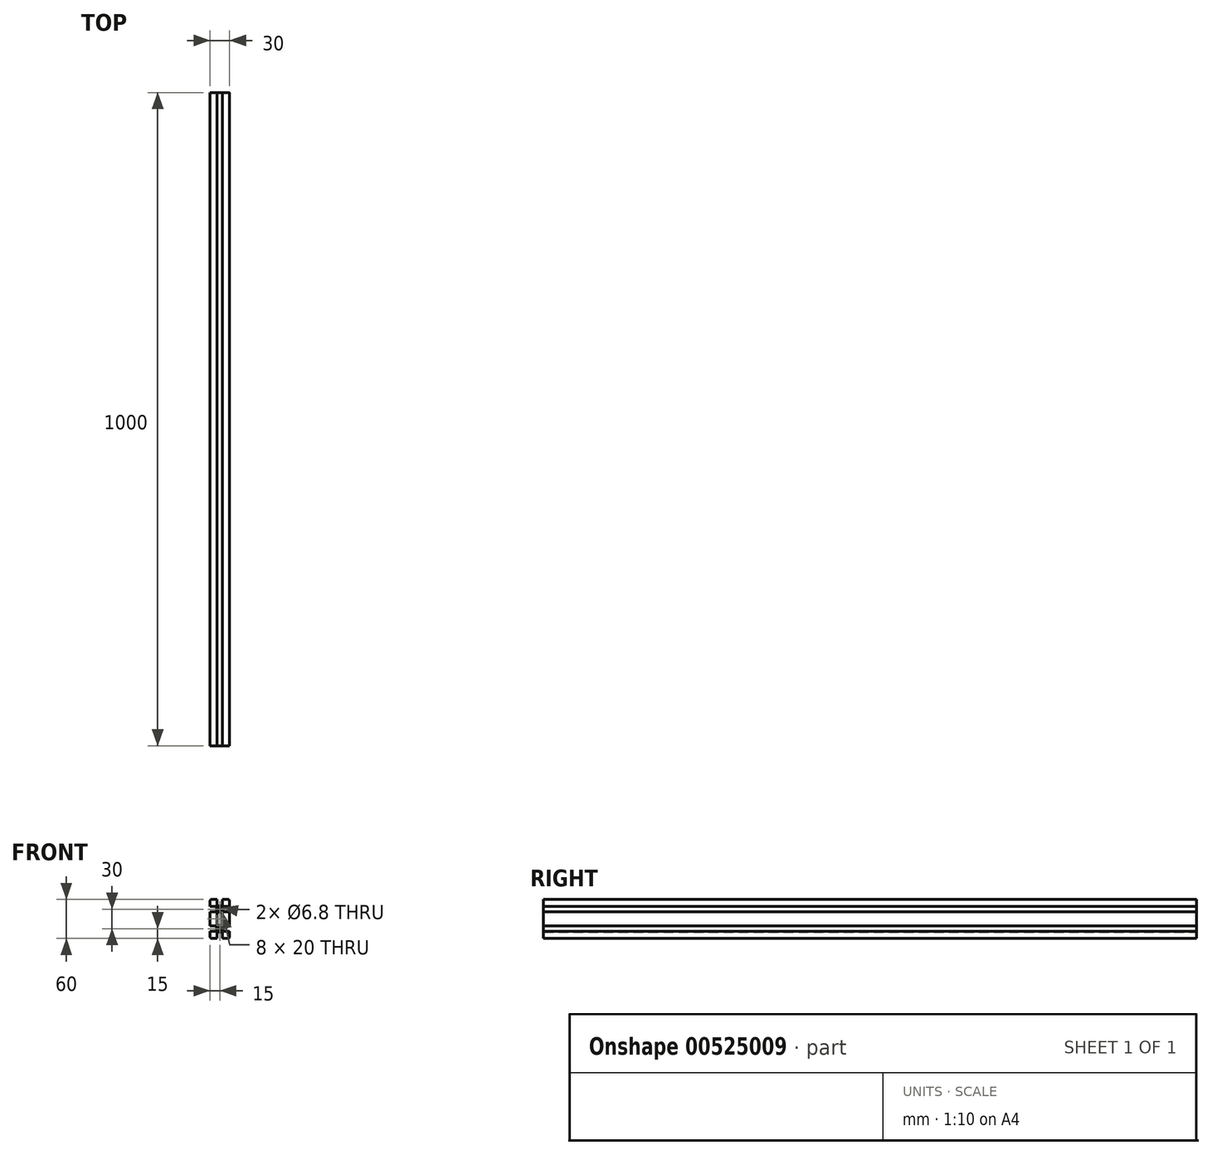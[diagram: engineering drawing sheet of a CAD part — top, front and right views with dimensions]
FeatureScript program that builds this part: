
annotation { "Feature Type Name" : "Feature", "Feature Type Description" : "" }
export const myFeature = defineFeature(function(context is Context, id is Id, definition is map)
    precondition{}
    {
        {
            var Q0;
            Q0=qCreatedBy(makeId("Front.planeOp"),FACE);
            var sketch = newSketch(context, id + "F0", { "sketchPlane" : qUnion([Q0])});
            skLineSegment(sketch, "E0.bottom", {"start": v(15, 30) * mm, "end": v(4, 30) * mm});
            skLineSegment(sketch, "E0.top", {"start": v(15, -30) * mm, "end": v(4, -30) * mm});
            skLineSegment(sketch, "E0.left", {"start": v(15, 30) * mm, "end": v(15, 19) * mm});
            skLineSegment(sketch, "E0.right", {"start": v(-15, 30) * mm, "end": v(-15, 19) * mm});
            skPoint(sketch, "E0.middle", {"position": v(0, 0) * mm});
            skLineSegment(sketch, "E1.top", {"start": v(-4, 20) * mm, "end": v(4, 20) * mm});
            skLineSegment(sketch, "E1.left", {"start": v(-4, 30) * mm, "end": v(-4, 20) * mm});
            skLineSegment(sketch, "E1.right", {"start": v(4, 30) * mm, "end": v(4, 20) * mm});
            skLineSegment(sketch, "E2.bottom", {"start": v(-15, 19) * mm, "end": v(-5, 19) * mm});
            skLineSegment(sketch, "E2.top", {"start": v(-15, 11) * mm, "end": v(-5, 11) * mm});
            skLineSegment(sketch, "E2.right", {"start": v(-5, 19) * mm, "end": v(-5, 11) * mm});
            skLineSegment(sketch, "E3.bottom", {"start": v(-15, -11) * mm, "end": v(-5, -11) * mm});
            skLineSegment(sketch, "E3.top", {"start": v(-15, -19) * mm, "end": v(-5, -19) * mm});
            skLineSegment(sketch, "E3.right", {"start": v(-5, -11) * mm, "end": v(-5, -19) * mm});
            skLineSegment(sketch, "E4.bottom", {"start": v(15, -11) * mm, "end": v(5, -11) * mm});
            skLineSegment(sketch, "E4.top", {"start": v(15, -19) * mm, "end": v(5, -19) * mm});
            skLineSegment(sketch, "E4.right", {"start": v(5, -11) * mm, "end": v(5, -19) * mm});
            skLineSegment(sketch, "E5.top", {"start": v(-4, -20) * mm, "end": v(4, -20) * mm});
            skLineSegment(sketch, "E5.left", {"start": v(-4, -30) * mm, "end": v(-4, -20) * mm});
            skLineSegment(sketch, "E5.right", {"start": v(4, -30) * mm, "end": v(4, -20) * mm});
            skLineSegment(sketch, "E6.bottom", {"start": v(15, 19) * mm, "end": v(5, 19) * mm});
            skLineSegment(sketch, "E6.top", {"start": v(15, 11) * mm, "end": v(5, 11) * mm});
            skLineSegment(sketch, "E6.right", {"start": v(5, 19) * mm, "end": v(5, 11) * mm});
            skLineSegment(sketch, "E7.trimOffspring", {"start": v(-15, -19) * mm, "end": v(-15, -30) * mm});
            skLineSegment(sketch, "E8.trimOffspring", {"start": v(-15, 11) * mm, "end": v(-15, -11) * mm});
            skLineSegment(sketch, "E9.trimOffspring", {"start": v(-4, 30) * mm, "end": v(-15, 30) * mm});
            skLineSegment(sketch, "E10.trimOffspring", {"start": v(15, 11) * mm, "end": v(15, -11) * mm});
            skLineSegment(sketch, "E11.trimOffspring", {"start": v(15, -19) * mm, "end": v(15, -30) * mm});
            skLineSegment(sketch, "E12.trimOffspring", {"start": v(-4, -30) * mm, "end": v(-15, -30) * mm});
            skSolve(sketch);
        }
        {
            var Q0;
            Q0 = qSketchRegion(id + "F0", true);
            extrude(context, id + "F1", {"entities" : qUnion([Q0]), "endBound" : BoundingType.SYMMETRIC, "depth" : 1000 * mm, "offsetDistance" : 25 * mm});
        }
        {
            var Q0;
            Q0=makeQuery(id+"F1.opExtrude","CAP_FACE",FACE,{"disambiguationData":[OSD([sQuery(id+"F0.wireOp",EDGE,"E0.bottom"),sQuery(id+"F0.wireOp",EDGE,"E0.top"),sQuery(id+"F0.wireOp",EDGE,"E0.left"),sQuery(id+"F0.wireOp",EDGE,"E0.right"),sQuery(id+"F0.wireOp",EDGE,"E1.top"),sQuery(id+"F0.wireOp",EDGE,"E1.left"),sQuery(id+"F0.wireOp",EDGE,"E1.right"),sQuery(id+"F0.wireOp",EDGE,"E2.bottom"),sQuery(id+"F0.wireOp",EDGE,"E2.top"),sQuery(id+"F0.wireOp",EDGE,"E2.right"),sQuery(id+"F0.wireOp",EDGE,"E3.bottom"),sQuery(id+"F0.wireOp",EDGE,"E3.top"),sQuery(id+"F0.wireOp",EDGE,"E3.right"),sQuery(id+"F0.wireOp",EDGE,"E4.bottom"),sQuery(id+"F0.wireOp",EDGE,"E4.top"),sQuery(id+"F0.wireOp",EDGE,"E4.right"),sQuery(id+"F0.wireOp",EDGE,"E5.top"),sQuery(id+"F0.wireOp",EDGE,"E5.left"),sQuery(id+"F0.wireOp",EDGE,"E5.right"),sQuery(id+"F0.wireOp",EDGE,"E6.bottom"),sQuery(id+"F0.wireOp",EDGE,"E6.top"),sQuery(id+"F0.wireOp",EDGE,"E6.right"),sQuery(id+"F0.wireOp",EDGE,"E7.trimOffspring"),sQuery(id+"F0.wireOp",EDGE,"E8.trimOffspring"),sQuery(id+"F0.wireOp",EDGE,"E9.trimOffspring"),sQuery(id+"F0.wireOp",EDGE,"E10.trimOffspring"),sQuery(id+"F0.wireOp",EDGE,"E11.trimOffspring"),sQuery(id+"F0.wireOp",EDGE,"E12.trimOffspring")])],"isStart":false});
            var sketch = newSketch(context, id + "F2", { "sketchPlane" : qUnion([Q0])});
            skPoint(sketch, "E13.centerSnap0", {"position": v(0, 20) * mm});
            skCircle(sketch, "E14", {"center": v(0, -15) * mm, "radius": 3.4 * mm});
            skLineSegment(sketch, "E15.bottom", {"start": v(4, 10) * mm, "end": v(-4, 10) * mm});
            skLineSegment(sketch, "E15.top", {"start": v(4, -10) * mm, "end": v(-4, -10) * mm});
            skLineSegment(sketch, "E15.left", {"start": v(4, 10) * mm, "end": v(4, -10) * mm});
            skLineSegment(sketch, "E15.right", {"start": v(-4, 10) * mm, "end": v(-4, -10) * mm});
            skPoint(sketch, "E15.middle", {"position": v(0, 0) * mm});
            skPoint(sketch, "E13.center.orphan", {"position": v(0, 15.6) * mm});
            skCircle(sketch, "E16", {"center": v(0, 15) * mm, "radius": 3.4 * mm});
            skSolve(sketch);
        }
        {
            var Q0;
            Q0 = qSketchRegion(id + "F2", true);
            extrude(context, id + "F3", {"entities" : qUnion([Q0]), "operationType" : NewBodyOperationType.REMOVE, "oppositeDirection" : true, "depth" : 1000 * mm, "offsetDistance" : 25 * mm});
        }
        {
            var Q0;
            Q0=makeQuery(id+"F1.opExtrude","SWEPT_EDGE",EDGE,{"disambiguationData":[OSD([sQuery(id+"F0.wireOp",EDGE,"E7.trimOffspring"),sQuery(id+"F0.wireOp",EDGE,"E12.trimOffspring")])]});
            var Q1;
            Q1=makeQuery(id+"F1.opExtrude","SWEPT_EDGE",EDGE,{"disambiguationData":[OSD([sQuery(id+"F0.wireOp",EDGE,"E0.top"),sQuery(id+"F0.wireOp",EDGE,"E11.trimOffspring")])]});
            var Q2;
            Q2=makeQuery(id+"F1.opExtrude","SWEPT_EDGE",EDGE,{"disambiguationData":[OSD([sQuery(id+"F0.wireOp",EDGE,"E0.bottom"),sQuery(id+"F0.wireOp",EDGE,"E0.left")])]});
            var Q3;
            Q3=makeQuery(id+"F1.opExtrude","SWEPT_EDGE",EDGE,{"disambiguationData":[OSD([sQuery(id+"F0.wireOp",EDGE,"E0.right"),sQuery(id+"F0.wireOp",EDGE,"E9.trimOffspring")])]});
            fillet(context, id + "F4", {"entities" : qUnion([Q0, Q1, Q2, Q3]), "radius" : 3 * mm, "tangentPropagation" : true, "allowEdgeOverflow" : false});
        }
    });
